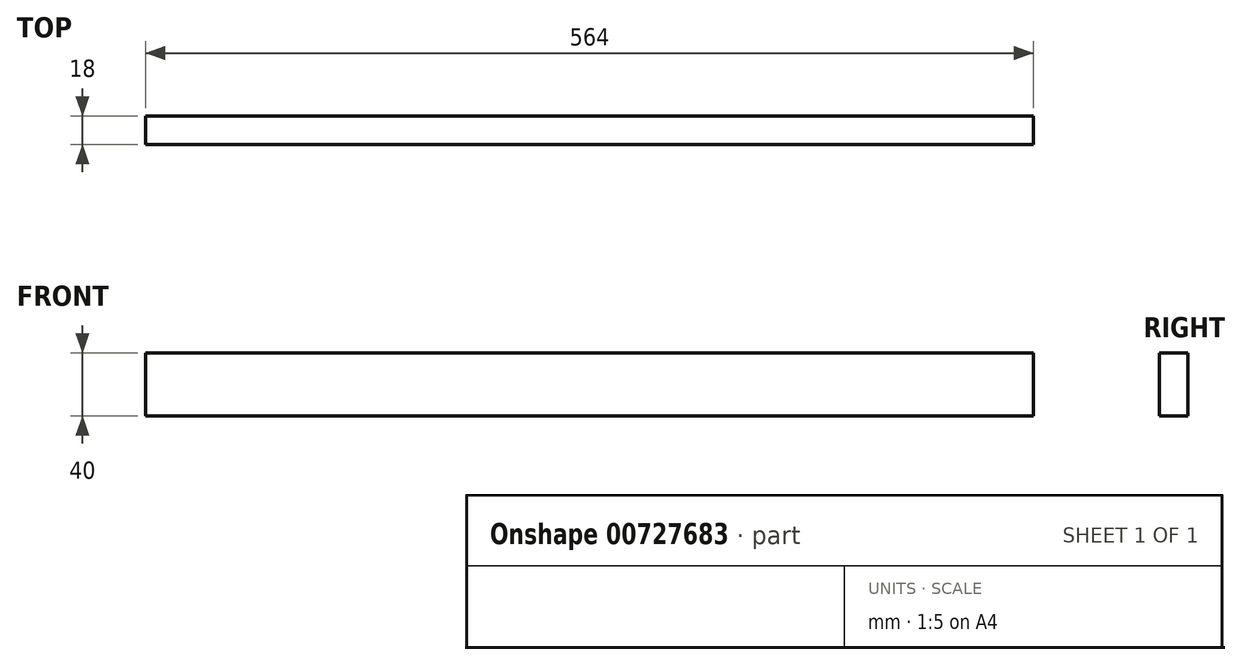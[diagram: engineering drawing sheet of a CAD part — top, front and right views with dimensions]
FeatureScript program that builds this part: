
annotation { "Feature Type Name" : "Feature", "Feature Type Description" : "" }
export const myFeature = defineFeature(function(context is Context, id is Id, definition is map)
    precondition{}
    {
        {
            var Q0;
            Q0=qCreatedBy(makeId("Front.planeOp"),FACE);
            var sketch = newSketch(context, id + "F0", { "sketchPlane" : qUnion([Q0])});
            skLineSegment(sketch, "E0.bottom", {"start": v(-282, 20) * mm, "end": v(282, 20) * mm});
            skLineSegment(sketch, "E0.top", {"start": v(-282, -20) * mm, "end": v(282, -20) * mm});
            skLineSegment(sketch, "E0.left", {"start": v(-282, 20) * mm, "end": v(-282, -20) * mm});
            skLineSegment(sketch, "E0.right", {"start": v(282, 20) * mm, "end": v(282, -20) * mm});
            skLineSegment(sketch, "E1", {"start": v(-282, 20) * mm, "end": v(282, -20) * mm, "construction": true});
            skSolve(sketch);
        }
        {
            var Q0;
            Q0 = qSketchRegion(id + "F0", true);
            extrude(context, id + "F1", {"entities" : qUnion([Q0]), "depth" : 18 * mm, "offsetDistance" : 25 * mm});
        }
    });
